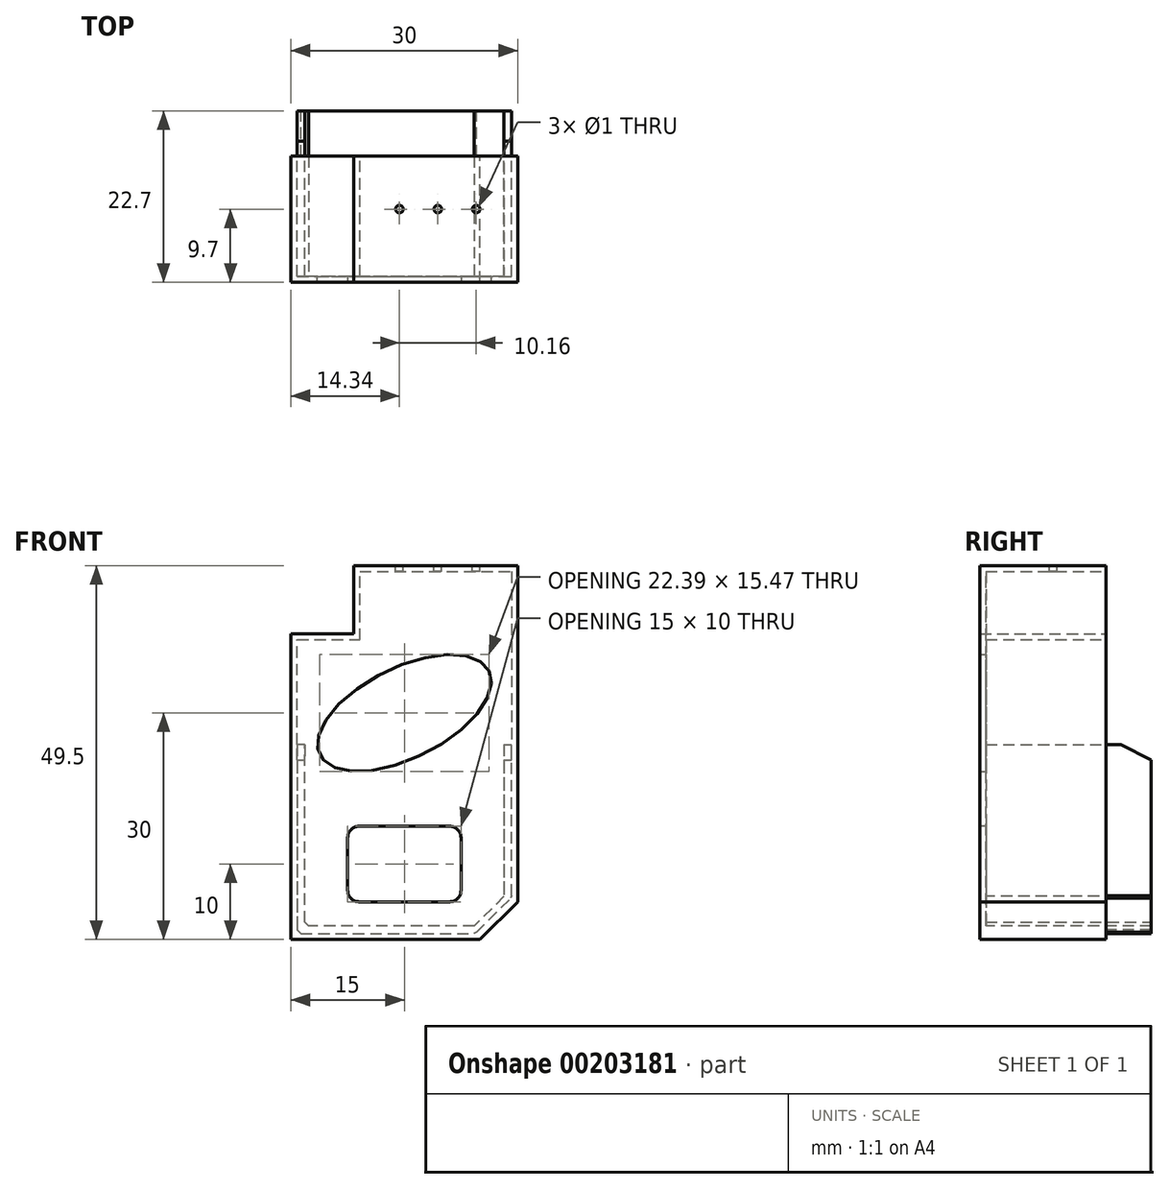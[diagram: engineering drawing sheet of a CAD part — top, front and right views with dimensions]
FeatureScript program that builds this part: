
annotation { "Feature Type Name" : "Feature", "Feature Type Description" : "" }
export const myFeature = defineFeature(function(context is Context, id is Id, definition is map)
    precondition{}
    {
        {
            assignVariable(context, id + "F0", {"name" : "epparoi", "anyValue" : 0.8});
        }
        {
            var Q0;
            Q0=qCreatedBy(makeId("Front.planeOp"),FACE);
            var sketch = newSketch(context, id + "F1", { "sketchPlane" : qUnion([Q0])});
            skLineSegment(sketch, "E0", {"start": v(0, 0) * mm, "end": v(0, 40.5) * mm});
            skLineSegment(sketch, "E1", {"start": v(0, 40.5) * mm, "end": v(8.3, 40.5) * mm});
            skLineSegment(sketch, "E2", {"start": v(8.3, 40.5) * mm, "end": v(8.3, 49.5) * mm});
            skLineSegment(sketch, "E3", {"start": v(8.3, 49.5) * mm, "end": v(30, 49.5) * mm});
            skLineSegment(sketch, "E4", {"start": v(30, 49.5) * mm, "end": v(30, 5) * mm});
            skLineSegment(sketch, "E5", {"start": v(30, 5) * mm, "end": v(25, 0) * mm});
            skLineSegment(sketch, "E6", {"start": v(25, 0) * mm, "end": v(0, 0) * mm});
            skSolve(sketch);
        }
        {
            var Q0;
            Q0=makeQuery(id+"F1.imprint","IMPRINT",FACE,{"disambiguationData":[TD([[makeQuery(id+"F1.imprint","IMPRINT",EDGE,{"derivedFrom":sQuery(id+"F1.wireOp",EDGE,"E0")}),-1.0]])]});
            extrude(context, id + "F2", {"entities" : qUnion([Q0]), "depth" : 16.7 * mm});
        }
        {
            var Q0;
            Q0=makeQuery(id+"F2.opExtrude","CAP_FACE",FACE,{"disambiguationData":[OSD([sQuery(id+"F1.wireOp",EDGE,"E0"),sQuery(id+"F1.wireOp",EDGE,"E1"),sQuery(id+"F1.wireOp",EDGE,"E2"),sQuery(id+"F1.wireOp",EDGE,"E3"),sQuery(id+"F1.wireOp",EDGE,"E4"),sQuery(id+"F1.wireOp",EDGE,"E5"),sQuery(id+"F1.wireOp",EDGE,"E6")])],"isStart":true});
            shell(context, id + "F3", {"entities" : qUnion([Q0]), "thickness" : (getVariable(context, 'epparoi')) * mm});
        }
        {
            var Q0;
            Q0=makeQuery(id+"F2.opExtrude","SWEPT_FACE",FACE,{"disambiguationData":[OSD([sQuery(id+"F1.wireOp",EDGE,"E3")])]});
            var sketch = newSketch(context, id + "F4", { "sketchPlane" : qUnion([Q0])});
            skPoint(sketch, "E7", {"position": v(24.5, -7) * mm});
            skPoint(sketch, "E8", {"position": v(19.42, -7) * mm});
            skPoint(sketch, "E9", {"position": v(14.34, -7) * mm});
            skSolve(sketch);
        }
        {
            var Q0;
            Q0=sQuery(id+"F4.wireOp",VERTEX,"E7");
            var Q1;
            Q1=sQuery(id+"F4.wireOp",VERTEX,"E8");
            var Q2;
            Q2=sQuery(id+"F4.wireOp",VERTEX,"E9");
            var Q3;
            Q3=makeQuery(id+"F2.opExtrude","SWEPT_BODY",BODY,{"disambiguationData":[OSD([sQuery(id+"F1.wireOp",EDGE,"E0"),sQuery(id+"F1.wireOp",EDGE,"E1"),sQuery(id+"F1.wireOp",EDGE,"E2"),sQuery(id+"F1.wireOp",EDGE,"E3"),sQuery(id+"F1.wireOp",EDGE,"E4"),sQuery(id+"F1.wireOp",EDGE,"E5"),sQuery(id+"F1.wireOp",EDGE,"E6")])]});
            hole(context, id + "F5", {"style" : HoleStyle.SIMPLE, "endStyle" : HoleEndStyle.BLIND, "holeDiameter" : 1 * mm, "holeDepth" : 20 * mm, "locations" : qUnion([Q0, Q1, Q2]), "scope" : qUnion([Q3])});
        }
        {
            var Q0;
            Q0=makeQuery(id+"F3.opShell","OFFSET_FACE",FACE,{"disambiguationData":[OSD([sQuery(id+"F1.wireOp",EDGE,"E0")])]});
            var sketch = newSketch(context, id + "F6", { "sketchPlane" : qUnion([Q0])});
            skLineSegment(sketch, "E10.bottom", {"start": v(-15.9, 0.8) * mm, "end": v(0, 0.8) * mm});
            skLineSegment(sketch, "E10.top", {"start": v(-15.9, 25.8) * mm, "end": v(0, 25.8) * mm});
            skLineSegment(sketch, "E10.left", {"start": v(-15.9, 0.8) * mm, "end": v(-15.9, 25.8) * mm});
            skLineSegment(sketch, "E10.right", {"start": v(0, 0.8) * mm, "end": v(0, 25.8) * mm});
            skSolve(sketch);
        }
        {
            var Q0;
            Q0=makeQuery(id+"F6.imprint","IMPRINT",FACE,{"disambiguationData":[TD([[makeQuery(id+"F6.imprint","IMPRINT",EDGE,{"derivedFrom":sQuery(id+"F6.wireOp",EDGE,"E10.bottom")}),1.0]])]});
            extrude(context, id + "F7", {"entities" : qUnion([Q0]), "operationType" : NewBodyOperationType.ADD, "depth" : 1 * mm});
        }
        {
            var Q0;
            Q0=makeQuery(id+"F3.opShell","OFFSET_FACE",FACE,{"disambiguationData":[OSD([sQuery(id+"F1.wireOp",EDGE,"E6")])]});
            extrude(context, id + "F8", {"entities" : qUnion([Q0]), "operationType" : NewBodyOperationType.ADD, "depth" : 1 * mm});
        }
        {
            var Q0;
            Q0=makeQuery(id+"F3.opShell","OFFSET_FACE",FACE,{"disambiguationData":[OSD([sQuery(id+"F1.wireOp",EDGE,"E4")])]});
            var sketch = newSketch(context, id + "F9", { "sketchPlane" : qUnion([Q0])});
            skLineSegment(sketch, "E11.bottom", {"start": v(15.9, 5.33) * mm, "end": v(0, 5.33) * mm});
            skLineSegment(sketch, "E11.top", {"start": v(15.9, 25.8) * mm, "end": v(0, 25.8) * mm});
            skLineSegment(sketch, "E11.left", {"start": v(15.9, 5.33) * mm, "end": v(15.9, 25.8) * mm});
            skLineSegment(sketch, "E11.right", {"start": v(0, 5.33) * mm, "end": v(0, 25.8) * mm});
            skSolve(sketch);
        }
        {
            var Q0;
            Q0=qSketchRegion(id+"F9",true);
            extrude(context, id + "F10", {"entities" : qUnion([Q0]), "operationType" : NewBodyOperationType.ADD, "depth" : 1 * mm});
        }
        {
            var Q0;
            Q0=makeQuery(id+"F3.opShell","OFFSET_FACE",FACE,{"disambiguationData":[OSD([sQuery(id+"F1.wireOp",EDGE,"E5")])]});
            extrude(context, id + "F11", {"entities" : qUnion([Q0]), "operationType" : NewBodyOperationType.ADD, "depth" : 1 * mm});
        }
        {
            var Q0;
            {var subQ0=sQuery(id+"F1.wireOp",EDGE,"E5");var subQ1=sQuery(id+"F1.wireOp",EDGE,"E6");Q0=makeQuery(id+"F11.boolean.opBoolean","MERGE",FACE,{"derivedFrom":[makeQuery(id+"F10.boolean.opBoolean","MERGE",FACE,{"derivedFrom":[makeQuery(id+"F8.boolean.opBoolean","MERGE",FACE,{"derivedFrom":[makeQuery(id+"F7.boolean.opBoolean","MERGE",FACE,{"derivedFrom":[makeQuery(id+"F2.opExtrude","CAP_FACE",FACE,{"disambiguationData":[OSD([sQuery(id+"F1.wireOp",EDGE,"E0"),sQuery(id+"F1.wireOp",EDGE,"E1"),sQuery(id+"F1.wireOp",EDGE,"E2"),sQuery(id+"F1.wireOp",EDGE,"E3"),sQuery(id+"F1.wireOp",EDGE,"E4"),subQ0,subQ1])],"isStart":true}),makeQuery(id+"F7.opExtrude","SWEPT_FACE",FACE,{"disambiguationData":[OSD([sQuery(id+"F6.wireOp",EDGE,"E10.right")])]})]}),makeQuery(id+"F8.opExtrude","SWEPT_FACE",FACE,{"disambiguationData":[OSD([subQ1]),TDD([makeQuery(id+"F3.opShell","OFFSET_EDGE",EDGE,{"disambiguationData":[OSD([subQ1]),TDD([makeQuery(id+"F2.opExtrude","CAP_EDGE",EDGE,{"disambiguationData":[OSD([subQ1])],"isStart":true})])]})])]})]}),makeQuery(id+"F10.opExtrude","SWEPT_FACE",FACE,{"disambiguationData":[OSD([sQuery(id+"F9.wireOp",EDGE,"E11.right")])]})]}),makeQuery(id+"F11.opExtrude","SWEPT_FACE",FACE,{"disambiguationData":[OSD([subQ0]),TDD([makeQuery(id+"F3.opShell","OFFSET_EDGE",EDGE,{"disambiguationData":[OSD([subQ0]),TDD([makeQuery(id+"F2.opExtrude","CAP_EDGE",EDGE,{"disambiguationData":[OSD([subQ0])],"isStart":true})])]})])]})]});}
            var sketch = newSketch(context, id + "F12", { "sketchPlane" : qUnion([Q0])});
            skLineSegment(sketch, "E12", {"start": v(-1.8, 25.8) * mm, "end": v(-0.8, 25.8) * mm});
            skLineSegment(sketch, "E13", {"start": v(-0.8, 25.8) * mm, "end": v(-0.8, 0.8) * mm});
            skLineSegment(sketch, "E14", {"start": v(-0.8, 0.8) * mm, "end": v(-24.39, 0.8) * mm});
            skLineSegment(sketch, "E15", {"start": v(-24.39, 0.8) * mm, "end": v(-29.2, 5.61) * mm});
            skLineSegment(sketch, "E16", {"start": v(-29.2, 5.61) * mm, "end": v(-29.2, 25.8) * mm});
            skLineSegment(sketch, "E17", {"start": v(-29.2, 25.8) * mm, "end": v(-28.2, 25.8) * mm});
            skLineSegment(sketch, "E18", {"start": v(-28.2, 25.8) * mm, "end": v(-28.2, 5.75) * mm});
            skLineSegment(sketch, "E19", {"start": v(-28.2, 5.75) * mm, "end": v(-24.25, 1.8) * mm});
            skLineSegment(sketch, "E20", {"start": v(-24.25, 1.8) * mm, "end": v(-1.8, 1.8) * mm});
            skLineSegment(sketch, "E21", {"start": v(-1.8, 1.8) * mm, "end": v(-1.8, 25.8) * mm});
            skSolve(sketch);
        }
        {
            var Q0;
            Q0=makeQuery(id+"F12.imprint","IMPRINT",FACE,{"disambiguationData":[TD([[makeQuery(id+"F12.imprint","IMPRINT",EDGE,{"derivedFrom":sQuery(id+"F12.wireOp",EDGE,"E12")}),-1.0]])]});
            extrude(context, id + "F13", {"entities" : qUnion([Q0]), "operationType" : NewBodyOperationType.ADD, "depth" : 6 * mm});
        }
        {
            var Q0;
            {var subQ0=sQuery(id+"F1.wireOp",EDGE,"E0");var subQ1=sQuery(id+"F1.wireOp",EDGE,"E4");var subQ2=sQuery(id+"F1.wireOp",EDGE,"E5");var subQ3=sQuery(id+"F1.wireOp",EDGE,"E6");var subQ4=sQuery(id+"F1.wireOp",EDGE,"E1");var subQ5=sQuery(id+"F1.wireOp",EDGE,"E2");var subQ6=sQuery(id+"F1.wireOp",EDGE,"E3");Q0=makeQuery(id+"F5UsCqK7vilbGDS_1.boolean.opBoolean","SPLIT",FACE,{"disambiguationData":[TD([makeQuery(id+"F2.opExtrude","SWEPT_FACE",FACE,{"disambiguationData":[OSD([subQ0])]})])],"derivedFrom":makeQuery(id+"F2.opExtrude","CAP_FACE",FACE,{"disambiguationData":[OSD([subQ0,subQ4,subQ5,subQ6,subQ1,subQ2,subQ3])],"isStart":false})});}
            var sketch = newSketch(context, id + "F14", { "sketchPlane" : qUnion([Q0])});
            skEllipse(sketch, "E22", {"center": v(15, 30) * mm, "majorRadius": 12.5 * mm, "minorRadius": 6 * mm, "majorAxis": v(0.9, 0.45)});
            skLineSegment(sketch, "E23.bottom", {"start": v(7.5, 15) * mm, "end": v(22.5, 15) * mm});
            skLineSegment(sketch, "E23.top", {"start": v(7.5, 5) * mm, "end": v(22.5, 5) * mm});
            skLineSegment(sketch, "E23.left", {"start": v(7.5, 15) * mm, "end": v(7.5, 5) * mm});
            skLineSegment(sketch, "E23.right", {"start": v(22.5, 15) * mm, "end": v(22.5, 5) * mm});
            skLineSegment(sketch, "E24", {"start": v(0, 20.25) * mm, "end": v(30, 20.25) * mm});
            skPoint(sketch, "E25", {"position": v(15, 15) * mm});
            skPoint(sketch, "E26", {"position": v(15, 20.25) * mm});
            skPoint(sketch, "E27", {"position": v(7.5, 10) * mm});
            skSolve(sketch);
        }
        {
            var Q0;
            Q0=makeQuery(id+"F14.imprint","IMPRINT",FACE,{"disambiguationData":[TD([[makeQuery(id+"F14.imprint","IMPRINT",EDGE,{"derivedFrom":sQuery(id+"F14.wireOp",EDGE,"E22")}),1.0]])]});
            var Q1;
            Q1=makeQuery(id+"F14.imprint","IMPRINT",FACE,{"disambiguationData":[TD([[makeQuery(id+"F14.imprint","IMPRINT",EDGE,{"derivedFrom":sQuery(id+"F14.wireOp",EDGE,"E23.bottom")}),-1.0]])]});
            extrude(context, id + "F15", {"entities" : qUnion([Q0, Q1]), "operationType" : NewBodyOperationType.REMOVE, "endBound" : BoundingType.THROUGH_ALL, "oppositeDirection" : true, "depth" : 3 * mm});
        }
        {
            var Q0;
            Q0=makeQuery(id+"F13.opExtrude","SWEPT_EDGE",EDGE,{"disambiguationData":[OSD([sQuery(id+"F12.wireOp",EDGE,"E15"),sQuery(id+"F12.wireOp",EDGE,"E16")])]});
            var Q1;
            Q1=makeQuery(id+"F13.opExtrude","SWEPT_EDGE",EDGE,{"disambiguationData":[OSD([sQuery(id+"F12.wireOp",EDGE,"E14"),sQuery(id+"F12.wireOp",EDGE,"E15")])]});
            var Q2;
            Q2=makeQuery(id+"F13.opExtrude","SWEPT_EDGE",EDGE,{"disambiguationData":[OSD([sQuery(id+"F12.wireOp",EDGE,"E13"),sQuery(id+"F12.wireOp",EDGE,"E14")])]});
            var Q3;
            Q3=makeQuery(id+"F13.boolean.opBoolean","MERGE",EDGE,{"derivedFrom":[makeQuery(id+"F8.opExtrude","CAP_EDGE",EDGE,{"disambiguationData":[OSD([sQuery(id+"F6.wireOp",EDGE,"E10.bottom")])],"isStart":false}),makeQuery(id+"F13.opExtrude","SWEPT_EDGE",EDGE,{"disambiguationData":[OSD([sQuery(id+"F12.wireOp",EDGE,"E20"),sQuery(id+"F12.wireOp",EDGE,"E21")])]})]});
            chamfer(context, id + "F16", {"entities" : qUnion([Q0, Q1, Q2, Q3]), "width" : 0.5 * mm, "tangentPropagation" : true});
        }
        {
            var Q0;
            Q0=makeQuery(id+"F13.opExtrude","CAP_EDGE",EDGE,{"disambiguationData":[OSD([sQuery(id+"F12.wireOp",EDGE,"E17")])],"isStart":false});
            var Q1;
            Q1=makeQuery(id+"F13.opExtrude","CAP_EDGE",EDGE,{"disambiguationData":[OSD([sQuery(id+"F12.wireOp",EDGE,"E12")])],"isStart":false});
            chamfer(context, id + "F17", {"entities" : qUnion([Q0, Q1]), "chamferType" : ChamferType.TWO_OFFSETS, "width1" : 4 * mm, "oppositeDirection" : true, "width2" : 2 * mm, "tangentPropagation" : true});
        }
        {
            var Q0;
            Q0=makeQuery(id+"F15.boolean.opBoolean","COPY",EDGE,{"derivedFrom":makeQuery(id+"F15.opExtrude","SWEPT_EDGE",EDGE,{"disambiguationData":[OSD([sQuery(id+"F14.wireOp",EDGE,"E23.bottom"),sQuery(id+"F14.wireOp",EDGE,"E23.right")])]})});
            var Q1;
            Q1=makeQuery(id+"F15.boolean.opBoolean","COPY",EDGE,{"derivedFrom":makeQuery(id+"F15.opExtrude","SWEPT_EDGE",EDGE,{"disambiguationData":[OSD([sQuery(id+"F14.wireOp",EDGE,"E23.bottom"),sQuery(id+"F14.wireOp",EDGE,"E23.left")])]})});
            var Q2;
            Q2=makeQuery(id+"F15.boolean.opBoolean","COPY",EDGE,{"derivedFrom":makeQuery(id+"F15.opExtrude","SWEPT_EDGE",EDGE,{"disambiguationData":[OSD([sQuery(id+"F14.wireOp",EDGE,"E23.top"),sQuery(id+"F14.wireOp",EDGE,"E23.left")])]})});
            var Q3;
            Q3=makeQuery(id+"F15.boolean.opBoolean","COPY",EDGE,{"derivedFrom":makeQuery(id+"F15.opExtrude","SWEPT_EDGE",EDGE,{"disambiguationData":[OSD([sQuery(id+"F14.wireOp",EDGE,"E23.top"),sQuery(id+"F14.wireOp",EDGE,"E23.right")])]})});
            fillet(context, id + "F18", {"entities" : qUnion([Q0, Q1, Q2, Q3]), "radius" : 1.5 * mm, "tangentPropagation" : true, "allowEdgeOverflow" : false});
        }
    });
